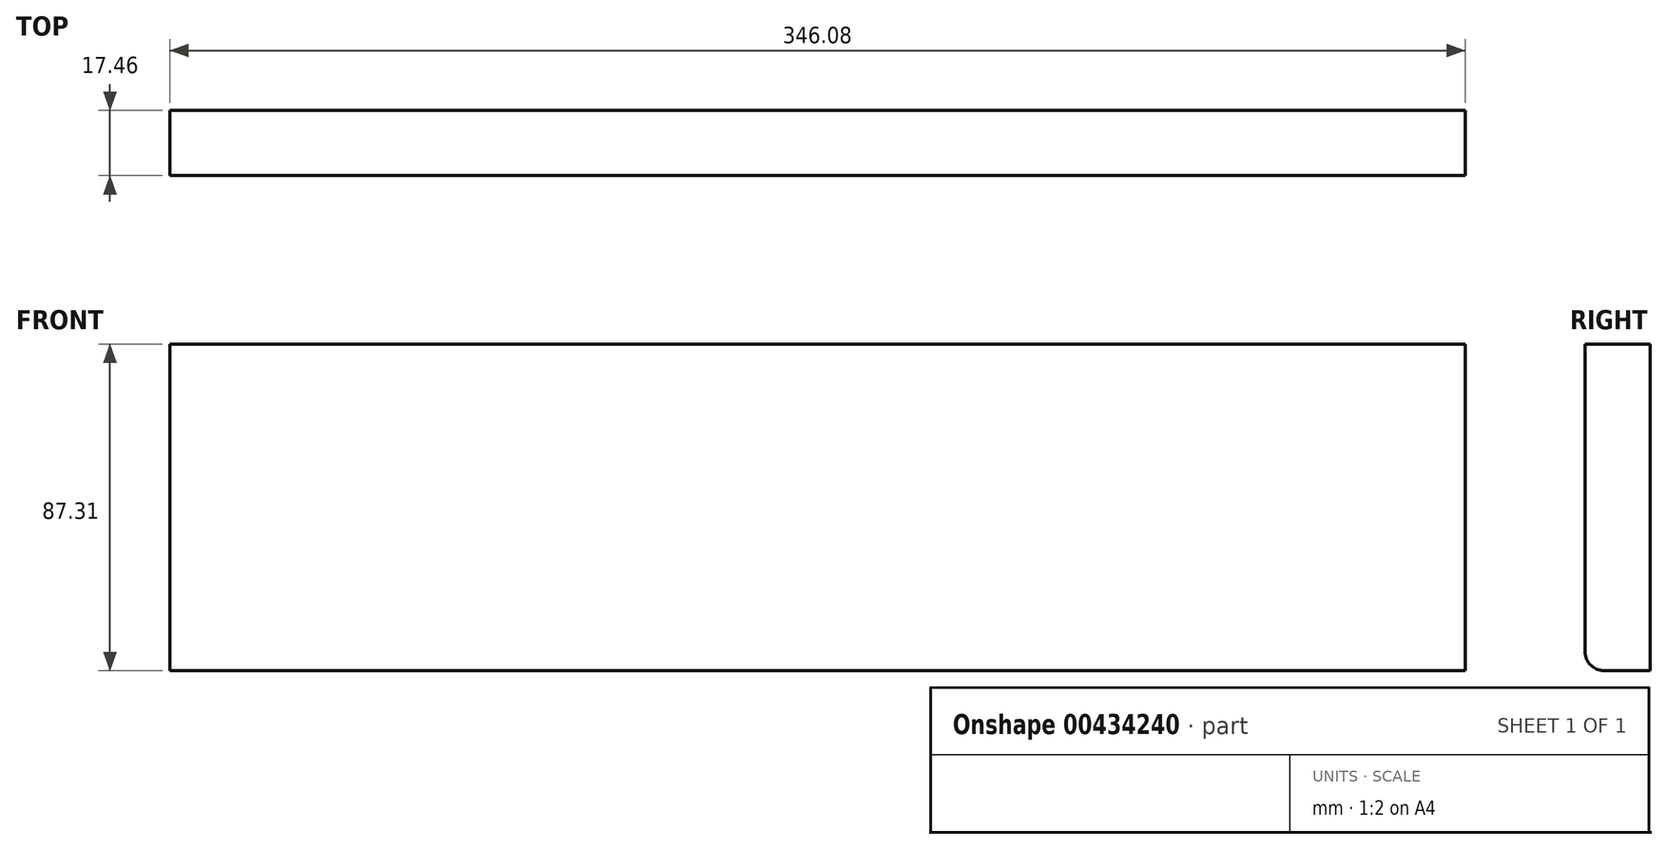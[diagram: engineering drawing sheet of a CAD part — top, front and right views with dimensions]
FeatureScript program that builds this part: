
annotation { "Feature Type Name" : "Feature", "Feature Type Description" : "" }
export const myFeature = defineFeature(function(context is Context, id is Id, definition is map)
    precondition{}
    {
        {
            var Q0;
            Q0=qCreatedBy(makeId("Front.planeOp"),FACE);
            var sketch = newSketch(context, id + "F0", { "sketchPlane" : qUnion([Q0])});
            skLineSegment(sketch, "E0.bottom", {"start": v(0, 0) * mm, "end": v(346.08, 0) * mm});
            skLineSegment(sketch, "E0.top", {"start": v(0, 87.31) * mm, "end": v(346.08, 87.31) * mm});
            skLineSegment(sketch, "E0.left", {"start": v(0, 0) * mm, "end": v(0, 87.31) * mm});
            skLineSegment(sketch, "E0.right", {"start": v(346.08, 0) * mm, "end": v(346.08, 87.31) * mm});
            skSolve(sketch);
        }
        {
            var Q0;
            Q0 = qSketchRegion(id + "F0", true);
            extrude(context, id + "F1", {"entities" : qUnion([Q0]), "depth" : 17.46 * mm});
        }
        {
            var Q0;
            Q0=makeQuery(id+"F1.opExtrude","CAP_EDGE",EDGE,{"disambiguationData":[OSD([sQuery(id+"F0.wireOp",EDGE,"E0.bottom")])],"isStart":false});
            fillet(context, id + "F2", {"entities" : qUnion([Q0]), "radius" : 5.08 * mm, "tangentPropagation" : true, "allowEdgeOverflow" : false});
        }
    });
